# Revit family: Levelers_Serco_Versadock
name_source: partatom
category: Generic Models
units: mm (PartAtom-declared; Revit-internal decimal feet)

## family parameters
Always vertical = Yes
Can host rebar = No
Cut with Voids When Loaded = No
Host = Floor
Maintain Annotation Orientation = No
Part Type = Normal
Room Calculation Point = No
Round Connector Dimension = Use Diameter
Shared = No

## types (6) — shared parameters
Capacity = 50/60/80k
Curb = 0' - 3"
Default Elevation = 0' - 0"
Description = 9' Wide, Integraterd Bumper Hydraulic Leveler
Manufacturer = Entrematic
Model = Versa Dock

## per-type parameters (varying)
| type | LipExtension | PitDepthF | PitDepthR | PitLength |
| 89 | 0' - 0" | 2' - 2" | 2' - 1" | 7' - 3" |
| 109 | 0' - 0" | 2' - 5" | 2' - 4" | 9' - 3" |
| 129 | 0' - 0" | 2' - 8" | 2' - 7" | 11' - 3" |
| 129 Barrier Lip | 0' - 5" | 2' - 8" | 2' - 7" | 11' - 3" |
| 89 Barrier Lip | 0' - 5" | 2' - 2" | 2' - 1" | 7' - 3" |
| 109 Barrier Lip | 0' - 5" | 2' - 5" | 2' - 4" | 9' - 3" |

## geometry (parser evidence)
native form markers: Sweep x3
no freeform markers — native parametric forms only
